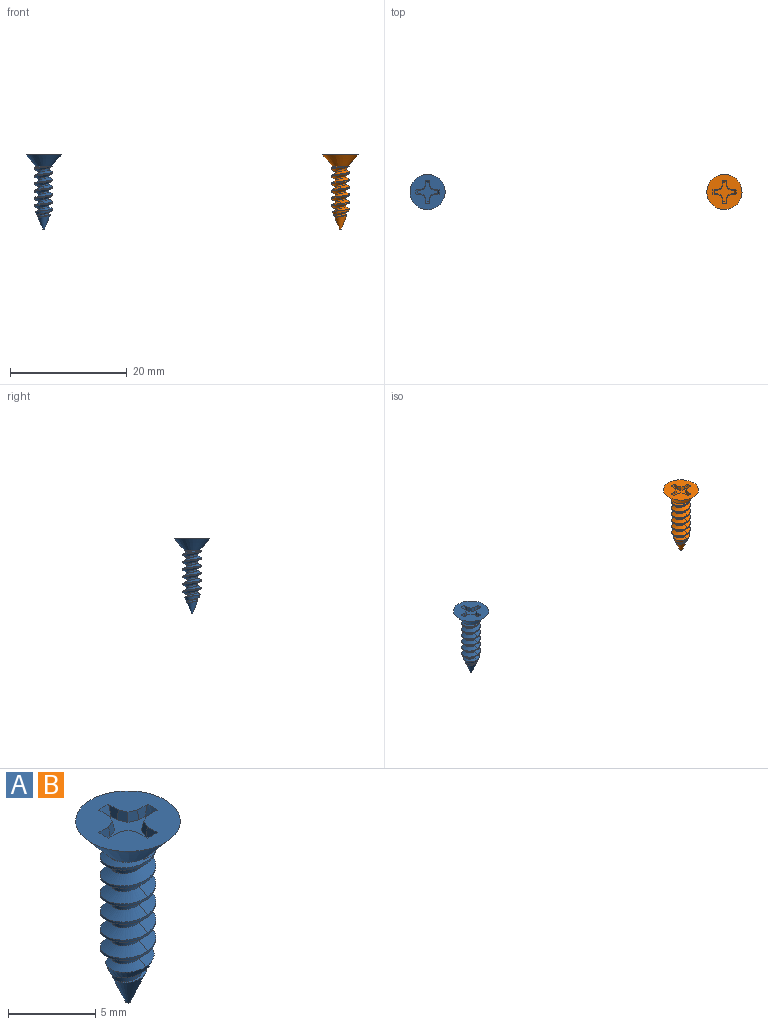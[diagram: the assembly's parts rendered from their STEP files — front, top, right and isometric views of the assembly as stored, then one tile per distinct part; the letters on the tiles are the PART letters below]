
ASSEMBLY  parts=2 mates=1
PART A: 45 faces, bbox 6.1x6.1x12.7 mm
  f0: torus R=2.75mm, axis (0,0,-1), area 3.7mm2, adj f4,f6,f13,f15,f16
  f1: cone r=2.01mm half-angle=25deg, axis (0,0,1), area 0.5mm2, adj f12,f28,f29,f40
  f2: cone r=1.59mm half-angle=22.5deg, axis (0,0,1), area 11.9mm2, adj f3,f6,f7,f8,f9,f10,f11,f23
  f3: cone r=1.59mm half-angle=22.5deg, axis (0,0,1), area 0.4mm2, adj f2,f5,f7,f8
  f4: cone r=3.01mm half-angle=41deg, axis (0,0,1), area 34.6mm2, adj f0,f12,f44
  f5: cylinder r=1.59mm len=7.27mm, axis (0,0,-1), area 9.1mm2, adj f3,f7,f8,f13,f14,f15,f16,f17
  f6: cylinder r=0.9mm len=7.72mm, axis (0,0,-1), area 10.9mm2, adj f0,f2,f7,f8,f9,f10,f11,f13
  f7: bspline ~3.17x3.17mm, area 5.5mm2, adj f2,f3,f5,f6,f9,f21
  f8: bspline ~3.17x3.17mm, area 6mm2, adj f2,f3,f5,f6,f10,f22
  f9: bspline ~3.21x3.18mm, area 0.7mm2, adj f2,f6,f7
  f10: bspline ~3.67x3.18mm, area 2.7mm2, adj f2,f6,f8,f11
  f11: bspline ~3.21x2.38mm, area 0.1mm2, adj f2,f6,f10
  f12: plane 6.02x6.02mm, normal (0,0,1), area 22mm2, adj f1,f4,f24,f25,f26,f27,f28,f30
  f13: bspline ~3.67x3.18mm, area 9mm2, adj f0,f5,f6,f16,f18
  f14: bspline ~3.18x3.17mm, area 9.4mm2, adj f5,f6,f15,f17
  f15: bspline ~3.18x3.17mm, area 4mm2, adj f0,f5,f6,f14,f44
  f16: bspline ~3.17x2.2mm, area 1.9mm2, adj f0,f5,f13,f44
  f17: bspline ~3.17x3.17mm, area 6.3mm2, adj f5,f6,f14,f20
  f18: bspline ~3.17x3.17mm, area 6.3mm2, adj f5,f6,f13,f19
  f19: bspline ~3.17x3.17mm, area 6.3mm2, adj f5,f6,f18,f22
  f20: bspline ~3.17x3.17mm, area 6.3mm2, adj f5,f6,f17,f21
  f21: bspline ~3.17x3.17mm, area 6.3mm2, adj f5,f6,f7,f20
  f22: bspline ~3.17x3.17mm, area 6.3mm2, adj f5,f6,f8,f19
  f23: plane 0.25x0.25mm, normal (0,0,-1), area 0.1mm2, adj f2
  f24: cone r=2.01mm half-angle=25deg, axis (0,0,1), area 0.5mm2, adj f12,f25,f29,f34
  f25: plane 0.81x0.64mm, normal (-0.98,0,0.17), area 0.4mm2, adj f12,f24,f26,f29
  f26: plane 0.64x0.64mm, normal (-0.91,-0.38,0.17), area 0.4mm2, adj f12,f25,f27,f29
  f27: plane 0.64x0.64mm, normal (-0.38,-0.91,0.17), area 0.4mm2, adj f12,f26,f28,f29
  f28: plane 0.81x0.64mm, normal (0,-0.98,0.17), area 0.4mm2, adj f1,f12,f27,f29
  f29: plane 3.42x3.42mm, normal (0,0,1), area 4.5mm2, adj f1,f24,f25,f26,f27,f28,f30,f31
  f30: cone r=2.01mm half-angle=25deg, axis (0,0,1), area 0.5mm2, adj f12,f29,f31,f39
  f31: plane 0.81x0.64mm, normal (0,-0.98,0.17), area 0.4mm2, adj f12,f29,f30,f32
  f32: plane 0.64x0.64mm, normal (0.38,-0.91,0.17), area 0.4mm2, adj f12,f29,f31,f33
  f33: plane 0.64x0.64mm, normal (0.91,-0.38,0.17), area 0.4mm2, adj f12,f29,f32,f34
  f34: plane 0.81x0.64mm, normal (0.98,0,0.17), area 0.4mm2, adj f12,f24,f29,f33
  f35: cone r=2.01mm half-angle=25deg, axis (0,0,1), area 0.5mm2, adj f12,f29,f36,f43
  f36: plane 0.81x0.64mm, normal (0.98,0,0.17), area 0.4mm2, adj f12,f29,f35,f37
  f37: plane 0.64x0.64mm, normal (0.91,0.38,0.17), area 0.4mm2, adj f12,f29,f36,f38
  f38: plane 0.64x0.64mm, normal (0.38,0.91,0.17), area 0.4mm2, adj f12,f29,f37,f39
  f39: plane 0.81x0.64mm, normal (0,0.98,0.17), area 0.4mm2, adj f12,f29,f30,f38
  f40: plane 0.81x0.64mm, normal (0,0.98,0.17), area 0.4mm2, adj f1,f12,f29,f41
  f41: plane 0.64x0.64mm, normal (-0.38,0.91,0.17), area 0.4mm2, adj f12,f29,f40,f42
  f42: plane 0.64x0.64mm, normal (-0.91,0.38,0.17), area 0.4mm2, adj f12,f29,f41,f43
  f43: plane 0.81x0.64mm, normal (-0.98,0,0.17), area 0.4mm2, adj f12,f29,f35,f42
  f44: plane 1.93x1.9mm, normal (0,0,1), area 0.5mm2, adj f4,f5,f15,f16
PART B: same geometry as A
PLACE A at identity
PLACE B t=(50.8,0,0)mm
MATE fastened B.f1 <-> A.f12  axis (0,0,1) through (50.8,0,1.91)mm
